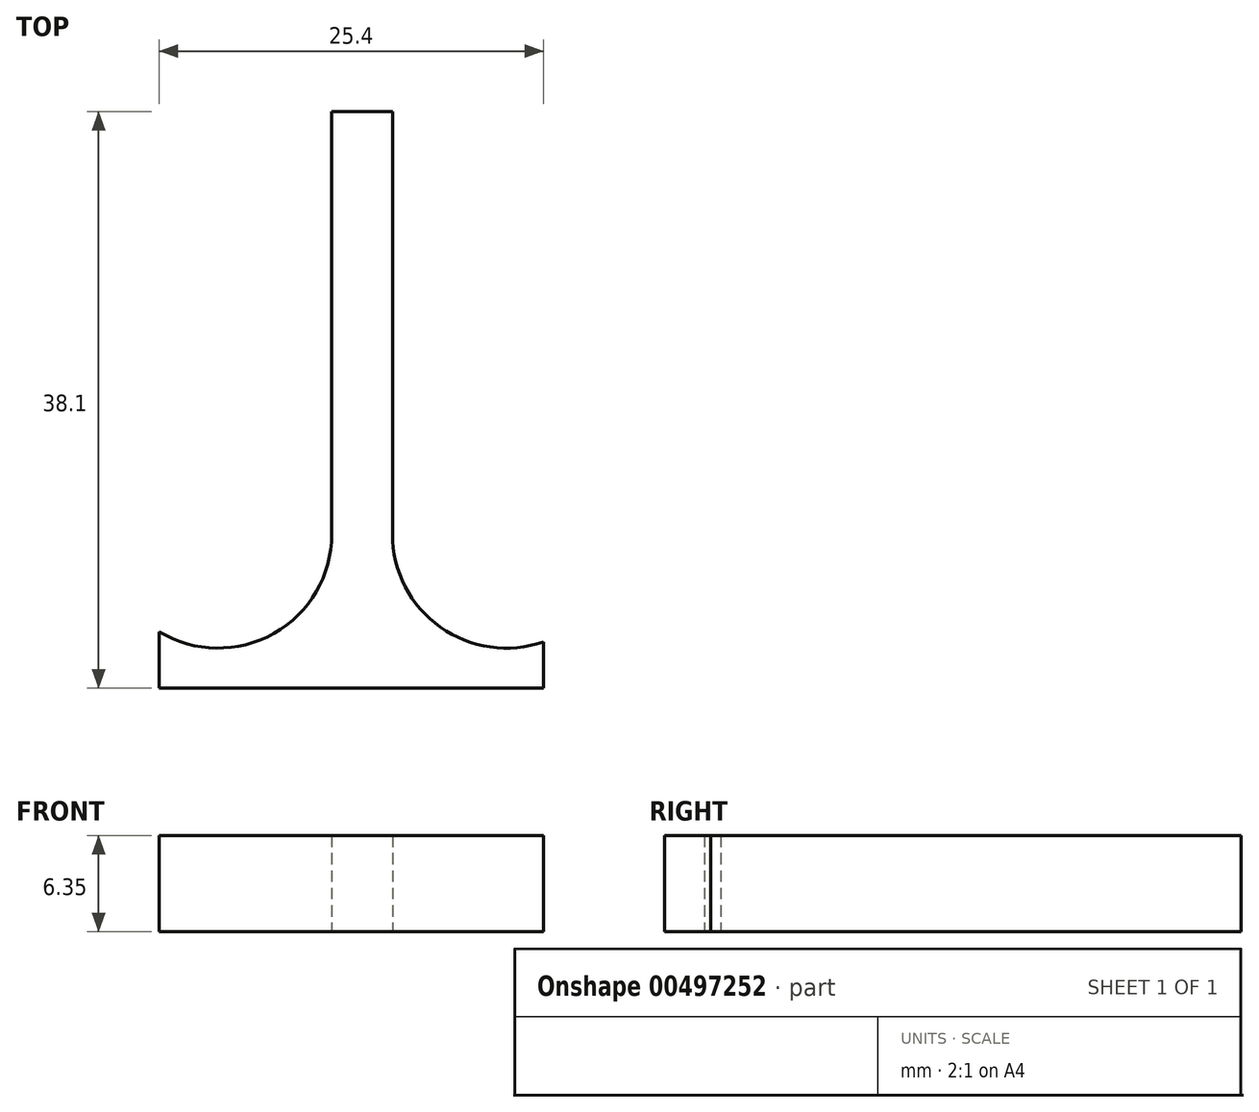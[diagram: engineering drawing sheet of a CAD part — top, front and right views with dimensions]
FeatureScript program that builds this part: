
annotation { "Feature Type Name" : "Feature", "Feature Type Description" : "" }
export const myFeature = defineFeature(function(context is Context, id is Id, definition is map)
    precondition{}
    {
        {
            var Q0;
            Q0=qCreatedBy(makeId("Top.planeOp"),FACE);
            var sketch = newSketch(context, id + "F0", { "sketchPlane" : qUnion([Q0])});
            skLineSegment(sketch, "E0.bottom", {"start": v(-0.49, 10.16) * mm, "end": v(3.53, 10.16) * mm});
            skLineSegment(sketch, "E0.top", {"start": v(-11.89, 0) * mm, "end": v(13.51, 0) * mm});
            skLineSegment(sketch, "E0.left", {"start": v(-11.89, 3.72) * mm, "end": v(-11.89, 0) * mm});
            skLineSegment(sketch, "E0.right", {"start": v(13.51, 3.06) * mm, "end": v(13.51, 0) * mm});
            skArc(sketch, "E1", {"start": v(-11.89, 3.72) * mm, "mid": v(-4.3, 3.61) * mm, "end": v(-0.49, 10.16) * mm});
            skArc(sketch, "E2", {"start": v(3.53, 10.16) * mm, "mid": v(6.69, 4.03) * mm, "end": v(13.51, 3.06) * mm});
            skLineSegment(sketch, "E3", {"start": v(-0.49, 10.16) * mm, "end": v(-0.49, 38.1) * mm});
            skLineSegment(sketch, "E4", {"start": v(3.53, 10.16) * mm, "end": v(3.53, 38.1) * mm});
            skLineSegment(sketch, "E5", {"start": v(3.53, 38.1) * mm, "end": v(-0.49, 38.1) * mm});
            skSolve(sketch);
        }
        {
            var Q0;
            Q0 = qSketchRegion(id + "F0", true);
            extrude(context, id + "F1", {"entities" : qUnion([Q0]), "depth" : 6.35 * mm, "offsetDistance" : 25.4 * mm});
        }
    });
